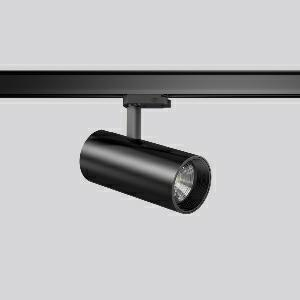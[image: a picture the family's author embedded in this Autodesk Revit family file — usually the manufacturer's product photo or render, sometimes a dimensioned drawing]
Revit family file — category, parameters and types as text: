
# Revit family: deecos_s_mini_742198_003_1_08ec
name_source: partatom
category: Lighting Fixtures
units: mm (PartAtom-declared; Revit-internal decimal feet)

## family parameters
Cut with Voids When Loaded = No
Host = Face
Light Source = No
Part Type = Normal
Room Calculation Point = No
Round Connector Dimension = Use Diameter
Shared = No

## types (1)
- DEECOS S mini (1 x LED Modul 940, 2400 lm, 4000)
    Apparent Load = 20 VA
    Approval mark = CE
    CIE Flux Codes = 99 100 100 100 100
    Color Rendering = 92
    Color Temperature = 4000
    Default Elevation = 1800 mm
    Description = Series: DEECOS S mini
LED surface-mounted projector in modern design with no visible cooling ribs. Housing: die-cast aluminium, powder-coated. Rotation range: 356°. Swivel range: 90°. Black plastic ring and recessed LED to prevent glare from the side. Optical assembly with lens made of plastic (polycarbonate) for the best homogeneous light distribution - can be changed without tools. Best colour rendering index Ra>90. With multi adaptor for 3-circuit tracks 230 V. Suitable for Track on ceiling, Wall track. High quality converter without flickering and stroboscopic effect. The following accessories can be mounted without use of tools: interchangeable lenses, decorative glasses, honeycomb louvre, clear and frosted diffusers, white interchangeable plastic ring. 
Colour: deep black, matt (RAL 9005)
Diameter: 87 mm
Height: 214 mm
Lamp: LED
Socket: without socket
Colour temperature: 4000K
Colour rendering index (CRI): 92
System power: 20 W
Rated luminous flux: 2400 lm
Luminous efficiency: 120 lm/W
Control gear: Regulated power supply
Protection class: I
Type of protection: IP 20
    Height = 214 mm
    Lamp = 1 x LED Modul 940
    Lamp Light Flux = 2400 lm
    Lamp count = 1
    Length = 87 mm
    Lifetime = 50000 h
    Luminous efficacy = 120 lm/W
    Manufacturer = RZB
    ModVariant = No
    Model = 742198.003.1
    Mounting Place = Ceiling
    Mounting Type = Rail mounted
    Number of Poles = 1
    OnlyDefault = Yes
    Power Factor = 1
    Product Name = DEECOS S mini
    Product group = Track mounted projectors
    ProductGroupID = 301
    Protection Class = Protection class I
    Protection Degree = IP 20
    RLX_Detail_Level = 1
    RLX_Emergency_Light_Flux = 0 lm
    RLX_Emergency_Type = 0
    RLX_Emergency_Type_DB = No
    RlxData = <blob elided: 39013 chars, md5=805df681>
    Socket = socket
    Standby Power = 0 W
    System Light Flux = 2400 lm
    System Power = 20 W
    Type Comments = Product without accessories
    Type Image = 741930.003.jpg
    URL = http://relux.com
    VarID = ---
    Voltage = 230 V
    Voltage Range = 220-240 V
    Weight = 0.00 kg
    Width = 0 mm  [stored 0 ft]

note: [stored X ft] marks values corroborated as IEEE doubles in the binary element streams (Revit-internal decimal feet)

## geometry (parser evidence)
native form markers: Blend x4, Sweep x10
no freeform markers — native parametric forms only
